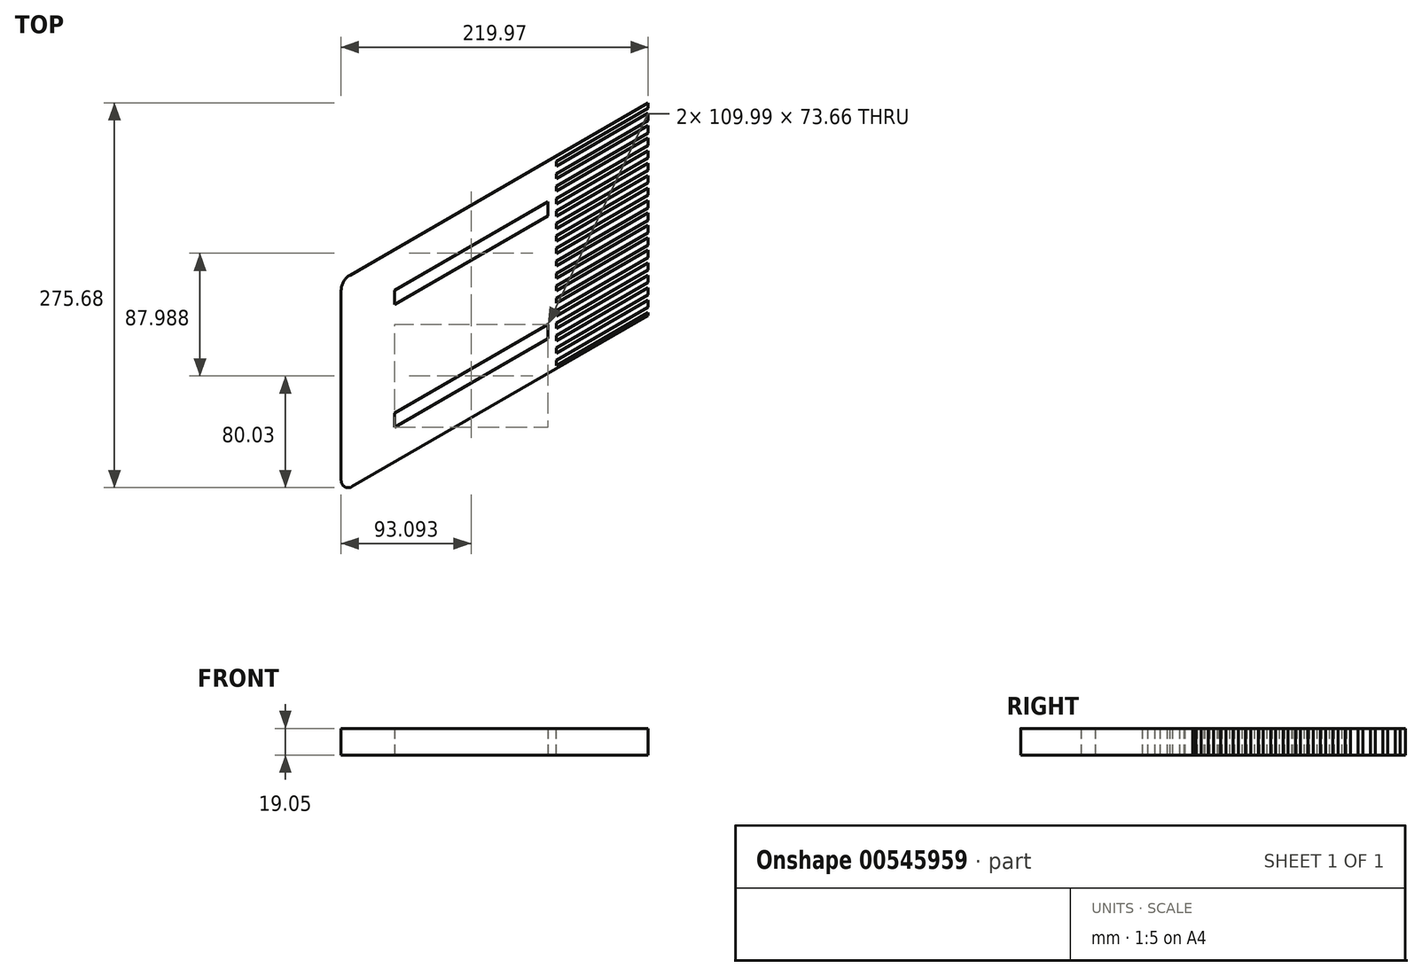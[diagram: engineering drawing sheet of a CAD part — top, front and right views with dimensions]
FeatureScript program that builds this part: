
annotation { "Feature Type Name" : "Feature", "Feature Type Description" : "" }
export const myFeature = defineFeature(function(context is Context, id is Id, definition is map)
    precondition{}
    {
        {
            var Q0;
            Q0=qCreatedBy(makeId("Top.planeOp"),FACE);
            var sketch = newSketch(context, id + "F0", { "sketchPlane" : qUnion([Q0])});
            skLineSegment(sketch, "E0", {"start": v(0, 0) * mm, "end": v(219.97, 127) * mm});
            skLineSegment(sketch, "E1", {"start": v(219.97, 127) * mm, "end": v(219.97, -25.4) * mm});
            skLineSegment(sketch, "E2", {"start": v(219.97, -25.4) * mm, "end": v(0, -152.4) * mm});
            skLineSegment(sketch, "E3", {"start": v(0, -152.4) * mm, "end": v(0, 0) * mm});
            skSolve(sketch);
        }
        {
            var Q0;
            Q0=makeQuery(id+"F0.imprint","IMPRINT",FACE,{"disambiguationData":[TD([[makeQuery(id+"F0.imprint","IMPRINT",EDGE,{"derivedFrom":sQuery(id+"F0.wireOp",EDGE,"E0")}),-1.0]])]});
            var sketch = newSketch(context, id + "F1", { "sketchPlane" : qUnion([Q0])});
            skLineSegment(sketch, "E4", {"start": v(38.1, -7.33) * mm, "end": v(148.09, 56.17) * mm});
            skLineSegment(sketch, "E5", {"start": v(148.09, 56.17) * mm, "end": v(148.09, 46) * mm});
            skLineSegment(sketch, "E6", {"start": v(148.09, 46) * mm, "end": v(38.1, -17.5) * mm});
            skLineSegment(sketch, "E7", {"start": v(38.1, -17.5) * mm, "end": v(38.1, -7.33) * mm});
            skLineSegment(sketch, "E8.1.0.0", {"start": v(148.09, -41.98) * mm, "end": v(38.1, -105.48) * mm});
            skLineSegment(sketch, "E8.1.0.1", {"start": v(148.09, -31.82) * mm, "end": v(148.09, -41.98) * mm});
            skLineSegment(sketch, "E8.1.0.2", {"start": v(38.1, -95.32) * mm, "end": v(148.09, -31.82) * mm});
            skLineSegment(sketch, "E8.1.0.3", {"start": v(38.1, -105.48) * mm, "end": v(38.1, -95.32) * mm});
            skSolve(sketch);
        }
        {
            var Q0;
            Q0 = qSketchRegion(id + "F0", true);
            extrude(context, id + "F2", {"entities" : qUnion([Q0]), "depth" : 19.05 * mm, "offsetDistance" : 25.4 * mm});
        }
        {
            var Q0;
            Q0 = qSketchRegion(id + "F1", true);
            extrude(context, id + "F3", {"entities" : qUnion([Q0]), "operationType" : NewBodyOperationType.REMOVE, "depth" : 25.4 * mm, "offsetDistance" : 25.4 * mm});
        }
        {
            var Q0;
            Q0=makeQuery(id+"F2.opExtrude","CAP_FACE",FACE,{"disambiguationData":[OSD([sQuery(id+"F0.wireOp",EDGE,"E0"),sQuery(id+"F0.wireOp",EDGE,"E1"),sQuery(id+"F0.wireOp",EDGE,"E2"),sQuery(id+"F0.wireOp",EDGE,"E3")])],"isStart":false});
            var sketch = newSketch(context, id + "F4", { "sketchPlane" : qUnion([Q0])});
            skLineSegment(sketch, "E9", {"start": v(219.97, 123.33) * mm, "end": v(153.98, 85.23) * mm});
            skLineSegment(sketch, "E10", {"start": v(153.98, 85.23) * mm, "end": v(153.98, 81.57) * mm});
            skLineSegment(sketch, "E11", {"start": v(153.98, 81.57) * mm, "end": v(219.97, 119.67) * mm});
            skLineSegment(sketch, "E12", {"start": v(219.97, 119.67) * mm, "end": v(219.97, 123.33) * mm});
            skLineSegment(sketch, "E13.1.0.0", {"start": v(153.98, 76.3) * mm, "end": v(153.98, 72.64) * mm});
            skLineSegment(sketch, "E13.1.0.1", {"start": v(153.98, 72.64) * mm, "end": v(219.97, 110.74) * mm});
            skLineSegment(sketch, "E13.1.0.2", {"start": v(219.97, 110.74) * mm, "end": v(219.97, 114.4) * mm});
            skLineSegment(sketch, "E13.1.0.3", {"start": v(219.97, 114.4) * mm, "end": v(153.98, 76.3) * mm});
            skLineSegment(sketch, "E13.2.0.0", {"start": v(153.98, 67.38) * mm, "end": v(153.98, 63.72) * mm});
            skLineSegment(sketch, "E13.2.0.1", {"start": v(153.98, 63.72) * mm, "end": v(219.97, 101.82) * mm});
            skLineSegment(sketch, "E13.2.0.2", {"start": v(219.97, 101.82) * mm, "end": v(219.97, 105.48) * mm});
            skLineSegment(sketch, "E13.2.0.3", {"start": v(219.97, 105.48) * mm, "end": v(153.98, 67.38) * mm});
            skLineSegment(sketch, "E13.3.0.0", {"start": v(153.98, 58.46) * mm, "end": v(153.98, 54.8) * mm});
            skLineSegment(sketch, "E13.3.0.1", {"start": v(153.98, 54.8) * mm, "end": v(219.97, 92.9) * mm});
            skLineSegment(sketch, "E13.3.0.2", {"start": v(219.97, 92.9) * mm, "end": v(219.97, 96.56) * mm});
            skLineSegment(sketch, "E13.3.0.3", {"start": v(219.97, 96.56) * mm, "end": v(153.98, 58.46) * mm});
            skLineSegment(sketch, "E13.4.0.0", {"start": v(153.98, 49.53) * mm, "end": v(153.98, 45.86) * mm});
            skLineSegment(sketch, "E13.4.0.1", {"start": v(153.98, 45.86) * mm, "end": v(219.97, 83.96) * mm});
            skLineSegment(sketch, "E13.4.0.2", {"start": v(219.97, 83.96) * mm, "end": v(219.97, 87.63) * mm});
            skLineSegment(sketch, "E13.4.0.3", {"start": v(219.97, 87.63) * mm, "end": v(153.98, 49.53) * mm});
            skLineSegment(sketch, "E13.5.0.0", {"start": v(153.98, 40.6) * mm, "end": v(153.98, 36.94) * mm});
            skLineSegment(sketch, "E13.5.0.1", {"start": v(153.98, 36.94) * mm, "end": v(219.97, 75.04) * mm});
            skLineSegment(sketch, "E13.5.0.2", {"start": v(219.97, 75.04) * mm, "end": v(219.97, 78.7) * mm});
            skLineSegment(sketch, "E13.5.0.3", {"start": v(219.97, 78.7) * mm, "end": v(153.98, 40.6) * mm});
            skLineSegment(sketch, "E13.6.0.0", {"start": v(153.98, 31.68) * mm, "end": v(153.98, 28.01) * mm});
            skLineSegment(sketch, "E13.6.0.1", {"start": v(153.98, 28.01) * mm, "end": v(219.97, 66.11) * mm});
            skLineSegment(sketch, "E13.6.0.2", {"start": v(219.97, 66.11) * mm, "end": v(219.97, 69.78) * mm});
            skLineSegment(sketch, "E13.6.0.3", {"start": v(219.97, 69.78) * mm, "end": v(153.98, 31.68) * mm});
            skLineSegment(sketch, "E13.7.0.0", {"start": v(153.98, 22.75) * mm, "end": v(153.98, 19.09) * mm});
            skLineSegment(sketch, "E13.7.0.1", {"start": v(153.98, 19.09) * mm, "end": v(219.97, 57.19) * mm});
            skLineSegment(sketch, "E13.7.0.2", {"start": v(219.97, 57.19) * mm, "end": v(219.97, 60.85) * mm});
            skLineSegment(sketch, "E13.7.0.3", {"start": v(219.97, 60.85) * mm, "end": v(153.98, 22.75) * mm});
            skLineSegment(sketch, "E13.8.0.0", {"start": v(153.98, 13.83) * mm, "end": v(153.98, 10.16) * mm});
            skLineSegment(sketch, "E13.8.0.1", {"start": v(153.98, 10.16) * mm, "end": v(219.97, 48.26) * mm});
            skLineSegment(sketch, "E13.8.0.2", {"start": v(219.97, 48.26) * mm, "end": v(219.97, 51.93) * mm});
            skLineSegment(sketch, "E13.8.0.3", {"start": v(219.97, 51.93) * mm, "end": v(153.98, 13.83) * mm});
            skLineSegment(sketch, "E13.9.0.0", {"start": v(153.98, 4.9) * mm, "end": v(153.98, 1.23) * mm});
            skLineSegment(sketch, "E13.9.0.1", {"start": v(153.98, 1.23) * mm, "end": v(219.97, 39.33) * mm});
            skLineSegment(sketch, "E13.9.0.2", {"start": v(219.97, 39.33) * mm, "end": v(219.97, 43) * mm});
            skLineSegment(sketch, "E13.9.0.3", {"start": v(219.97, 43) * mm, "end": v(153.98, 4.9) * mm});
            skLineSegment(sketch, "E13.10.0.0", {"start": v(153.98, -4.02) * mm, "end": v(153.98, -7.7) * mm});
            skLineSegment(sketch, "E13.10.0.1", {"start": v(153.98, -7.7) * mm, "end": v(219.97, 30.4) * mm});
            skLineSegment(sketch, "E13.10.0.2", {"start": v(219.97, 30.4) * mm, "end": v(219.97, 34.08) * mm});
            skLineSegment(sketch, "E13.10.0.3", {"start": v(219.97, 34.08) * mm, "end": v(153.98, -4.02) * mm});
            skLineSegment(sketch, "E13.11.0.0", {"start": v(153.98, -12.95) * mm, "end": v(153.98, -16.62) * mm});
            skLineSegment(sketch, "E13.11.0.1", {"start": v(153.98, -16.62) * mm, "end": v(219.97, 21.48) * mm});
            skLineSegment(sketch, "E13.11.0.2", {"start": v(219.97, 21.48) * mm, "end": v(219.97, 25.15) * mm});
            skLineSegment(sketch, "E13.11.0.3", {"start": v(219.97, 25.15) * mm, "end": v(153.98, -12.95) * mm});
            skLineSegment(sketch, "E13.12.0.0", {"start": v(153.98, -21.88) * mm, "end": v(153.98, -25.54) * mm});
            skLineSegment(sketch, "E13.12.0.1", {"start": v(153.98, -25.54) * mm, "end": v(219.97, 12.56) * mm});
            skLineSegment(sketch, "E13.12.0.2", {"start": v(219.97, 12.56) * mm, "end": v(219.97, 16.22) * mm});
            skLineSegment(sketch, "E13.12.0.3", {"start": v(219.97, 16.22) * mm, "end": v(153.98, -21.88) * mm});
            skLineSegment(sketch, "E13.13.0.0", {"start": v(153.98, -30.8) * mm, "end": v(153.98, -34.47) * mm});
            skLineSegment(sketch, "E13.13.0.1", {"start": v(153.98, -34.47) * mm, "end": v(219.97, 3.63) * mm});
            skLineSegment(sketch, "E13.13.0.2", {"start": v(219.97, 3.63) * mm, "end": v(219.97, 7.3) * mm});
            skLineSegment(sketch, "E13.13.0.3", {"start": v(219.97, 7.3) * mm, "end": v(153.98, -30.8) * mm});
            skLineSegment(sketch, "E13.14.0.0", {"start": v(153.98, -39.73) * mm, "end": v(153.98, -43.4) * mm});
            skLineSegment(sketch, "E13.14.0.1", {"start": v(153.98, -43.4) * mm, "end": v(219.97, -5.3) * mm});
            skLineSegment(sketch, "E13.14.0.2", {"start": v(219.97, -5.3) * mm, "end": v(219.97, -1.63) * mm});
            skLineSegment(sketch, "E13.14.0.3", {"start": v(219.97, -1.63) * mm, "end": v(153.98, -39.73) * mm});
            skLineSegment(sketch, "E13.15.0.0", {"start": v(153.98, -48.65) * mm, "end": v(153.98, -52.32) * mm});
            skLineSegment(sketch, "E13.15.0.1", {"start": v(153.98, -52.32) * mm, "end": v(219.97, -14.22) * mm});
            skLineSegment(sketch, "E13.15.0.2", {"start": v(219.97, -14.22) * mm, "end": v(219.97, -10.55) * mm});
            skLineSegment(sketch, "E13.15.0.3", {"start": v(219.97, -10.55) * mm, "end": v(153.98, -48.65) * mm});
            skLineSegment(sketch, "E13.16.0.0", {"start": v(153.98, -57.58) * mm, "end": v(153.98, -61.25) * mm});
            skLineSegment(sketch, "E13.16.0.1", {"start": v(153.98, -61.25) * mm, "end": v(219.97, -23.15) * mm});
            skLineSegment(sketch, "E13.16.0.2", {"start": v(219.97, -23.15) * mm, "end": v(219.97, -19.48) * mm});
            skLineSegment(sketch, "E13.16.0.3", {"start": v(219.97, -19.48) * mm, "end": v(153.98, -57.58) * mm});
            skLineSegment(sketch, "E13.17.0.0", {"start": v(153.98, -66.5) * mm, "end": v(153.98, -70.17) * mm});
            skLineSegment(sketch, "E13.17.0.1", {"start": v(153.98, -70.17) * mm, "end": v(219.97, -32.07) * mm});
            skLineSegment(sketch, "E13.17.0.2", {"start": v(219.97, -32.07) * mm, "end": v(219.97, -28.4) * mm});
            skLineSegment(sketch, "E13.17.0.3", {"start": v(219.97, -28.4) * mm, "end": v(153.98, -66.5) * mm});
            skLineSegment(sketch, "E13.18.0.0", {"start": v(153.98, -75.43) * mm, "end": v(153.98, -79.1) * mm});
            skLineSegment(sketch, "E13.18.0.1", {"start": v(153.98, -79.1) * mm, "end": v(219.97, -41) * mm});
            skLineSegment(sketch, "E13.18.0.2", {"start": v(219.97, -41) * mm, "end": v(219.97, -37.33) * mm});
            skLineSegment(sketch, "E13.18.0.3", {"start": v(219.97, -37.33) * mm, "end": v(153.98, -75.43) * mm});
            skLineSegment(sketch, "E13.direction1", {"start": v(153.98, 81.57) * mm, "end": v(153.98, 72.64) * mm, "construction": true});
            skSolve(sketch);
        }
        {
            var Q0;
            Q0 = qSketchRegion(id + "F4", true);
            extrude(context, id + "F5", {"entities" : qUnion([Q0]), "operationType" : NewBodyOperationType.REMOVE, "oppositeDirection" : true, "depth" : 25.4 * mm, "offsetDistance" : 25.4 * mm});
        }
        {
            var Q0;
            Q0=makeQuery(id+"F2.opExtrude","SWEPT_EDGE",EDGE,{"disambiguationData":[OSD([sQuery(id+"F0.wireOp",EDGE,"E0"),sQuery(id+"F0.wireOp",EDGE,"E3")])]});
            fillet(context, id + "F6", {"entities" : qUnion([Q0]), "radius" : 12.7 * mm, "tangentPropagation" : true, "allowEdgeOverflow" : false});
        }
        {
            var Q0;
            Q0=makeQuery(id+"F2.opExtrude","SWEPT_EDGE",EDGE,{"disambiguationData":[OSD([sQuery(id+"F0.wireOp",EDGE,"E2"),sQuery(id+"F0.wireOp",EDGE,"E3")])]});
            fillet(context, id + "F7", {"entities" : qUnion([Q0]), "radius" : 5.08 * mm, "tangentPropagation" : true, "allowEdgeOverflow" : false});
        }
    });
